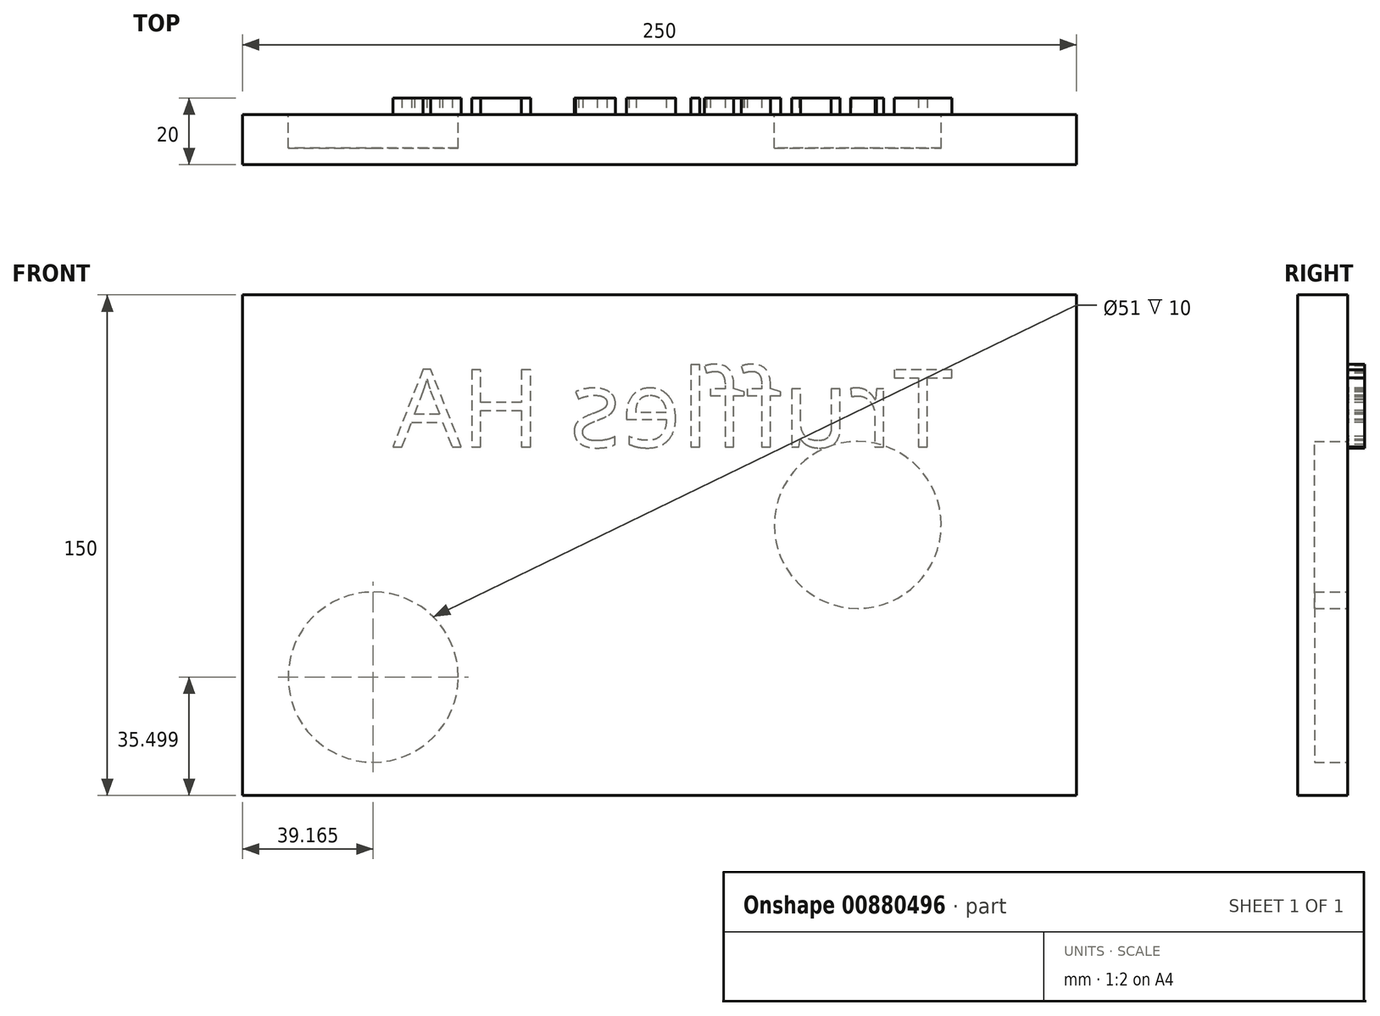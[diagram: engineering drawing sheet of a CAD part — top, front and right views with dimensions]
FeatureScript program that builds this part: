
annotation { "Feature Type Name" : "Feature", "Feature Type Description" : "" }
export const myFeature = defineFeature(function(context is Context, id is Id, definition is map)
    precondition{}
    {
        {
            var Q0;
            Q0=qCreatedBy(makeId("Front.planeOp"),FACE);
            var sketch = newSketch(context, id + "F0", { "sketchPlane" : qUnion([Q0])});
            skLineSegment(sketch, "E0.bottom", {"start": v(-120.42, 81.56) * mm, "end": v(129.58, 81.56) * mm});
            skLineSegment(sketch, "E0.top", {"start": v(-120.42, -68.44) * mm, "end": v(129.58, -68.44) * mm});
            skLineSegment(sketch, "E0.left", {"start": v(-120.42, 81.56) * mm, "end": v(-120.42, -68.44) * mm});
            skLineSegment(sketch, "E0.right", {"start": v(129.58, 81.56) * mm, "end": v(129.58, -68.44) * mm});
            skSolve(sketch);
        }
        {
            var Q0;
            Q0 = qSketchRegion(id + "F0", true);
            extrude(context, id + "F1", {"entities" : qUnion([Q0]), "depth" : 15 * mm, "offsetDistance" : 25 * mm});
        }
        {
            var Q0;
            Q0=makeQuery(id+"F1.opExtrude","CAP_FACE",FACE,{"disambiguationData":[OSD([sQuery(id+"F0.wireOp",EDGE,"E0.bottom"),sQuery(id+"F0.wireOp",EDGE,"E0.top"),sQuery(id+"F0.wireOp",EDGE,"E0.left"),sQuery(id+"F0.wireOp",EDGE,"E0.right")])],"isStart":true});
            var sketch = newSketch(context, id + "F2", { "sketchPlane" : qUnion([Q0])});
            skCircle(sketch, "E1", {"center": v(81.26, -32.94) * mm, "radius": 25.5 * mm});
            skSolve(sketch);
        }
        {
            var Q0;
            Q0 = qSketchRegion(id + "F2", true);
            extrude(context, id + "F3", {"entities" : qUnion([Q0]), "operationType" : NewBodyOperationType.REMOVE, "oppositeDirection" : true, "depth" : 10 * mm, "offsetDistance" : 25 * mm});
        }
        {
            var Q0;
            Q0=makeQuery(id+"F1.opExtrude","CAP_FACE",FACE,{"disambiguationData":[OSD([sQuery(id+"F0.wireOp",EDGE,"E0.bottom"),sQuery(id+"F0.wireOp",EDGE,"E0.top"),sQuery(id+"F0.wireOp",EDGE,"E0.left"),sQuery(id+"F0.wireOp",EDGE,"E0.right")])],"isStart":true});
            var sketch = newSketch(context, id + "F4", { "sketchPlane" : qUnion([Q0])});
            skText(sketch, "E2", { "text": "Truffles HA", "fontName": "OpenSans-Regular.ttf"});
            const initialGuessF4  = {"E2": [-0.09251, 0.03599, 1, 0, 0.02336]};
            skSetInitialGuess(sketch, initialGuessF4);
            skSolve(sketch);
        }
        {
            var Q0;
            Q0 = qSketchRegion(id + "F4", true);
            extrude(context, id + "F5", {"entities" : qUnion([Q0]), "operationType" : NewBodyOperationType.ADD, "depth" : 5 * mm, "offsetDistance" : 25 * mm});
        }
        {
            var Q0;
            Q0=qCreatedBy(makeId("Front.planeOp"),FACE);
            var sketch = newSketch(context, id + "F6", { "sketchPlane" : qUnion([Q0])});
            skCircle(sketch, "E3", {"center": v(63.98, 12.63) * mm, "radius": 25 * mm});
            skSolve(sketch);
        }
        {
            var Q0;
            Q0 = qSketchRegion(id + "F6", true);
            extrude(context, id + "F7", {"entities" : qUnion([Q0]), "depth" : 10 * mm, "offsetDistance" : 25 * mm});
        }
    });
